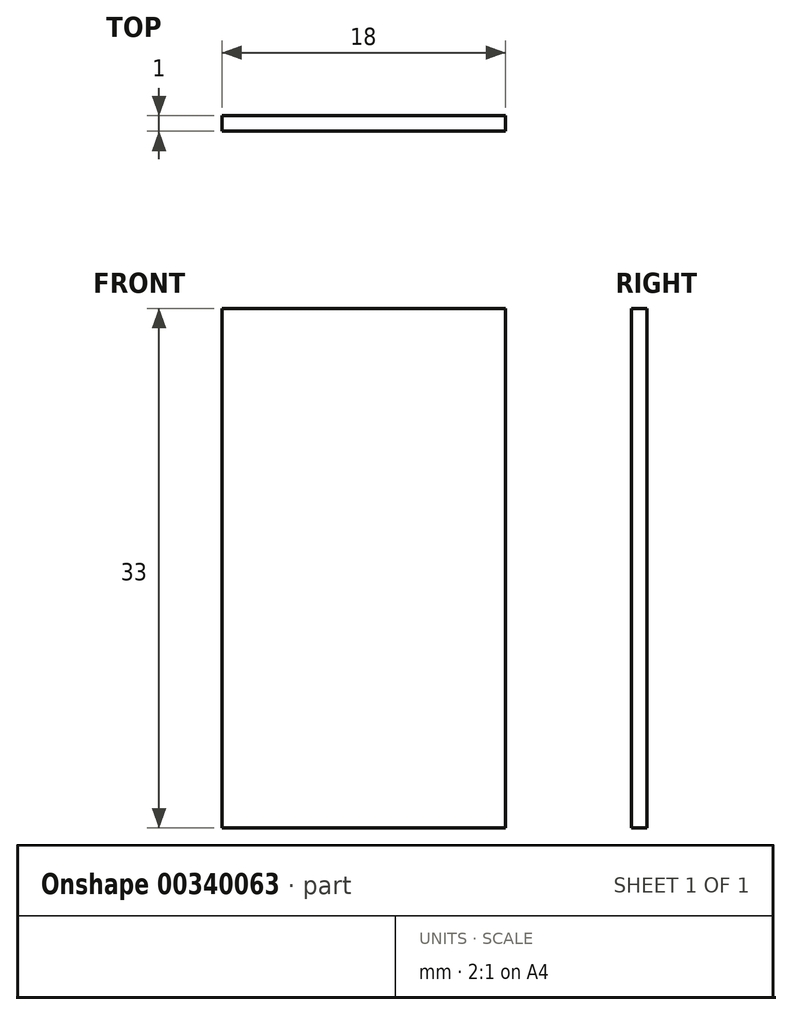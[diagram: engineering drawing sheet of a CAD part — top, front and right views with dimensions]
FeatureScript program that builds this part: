
annotation { "Feature Type Name" : "Feature", "Feature Type Description" : "" }
export const myFeature = defineFeature(function(context is Context, id is Id, definition is map)
    precondition{}
    {
        {
            var Q0;
            Q0=qCreatedBy(makeId("Front.planeOp"),FACE);
            var sketch = newSketch(context, id + "F0", { "sketchPlane" : qUnion([Q0])});
            skLineSegment(sketch, "E0", {"start": v(0, 0) * mm, "end": v(18, 0) * mm});
            skLineSegment(sketch, "E1", {"start": v(18, 0) * mm, "end": v(18, -33) * mm});
            skLineSegment(sketch, "E2", {"start": v(18, -33) * mm, "end": v(0, -33) * mm});
            skLineSegment(sketch, "E3", {"start": v(0, -33) * mm, "end": v(0, 0) * mm});
            skSolve(sketch);
        }
        {
            var Q0;
            Q0 = qSketchRegion(id + "F0", true);
            extrude(context, id + "F1", {"entities" : qUnion([Q0]), "oppositeDirection" : true, "depth" : 1 * mm});
        }
    });
